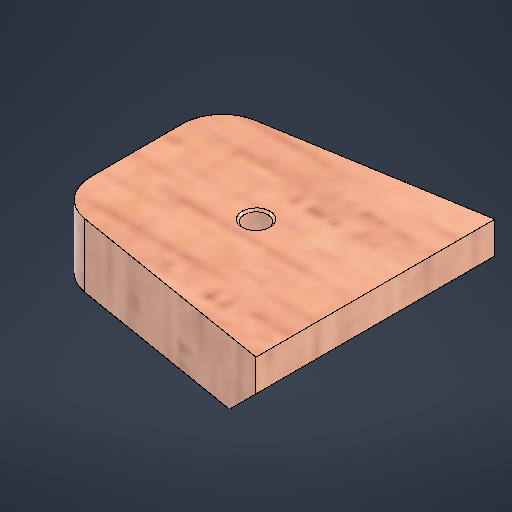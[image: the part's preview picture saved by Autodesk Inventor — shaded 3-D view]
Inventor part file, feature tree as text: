
AUTODESK INVENTOR PART (.ipt)
format: ipt  version: 2025.3 (Build 293356000, 356)  size: 276,480 bytes
history: native  units: mm
features: chamfer x2, sketch x1, extrude x1, hole x1, fillet x1
ambient origin geometry x8: Origin, YZ Plane, XZ Plane, XY Plane, X Axis, Y Axis, Z Axis, Center Point
bodies: Solid1 (feature_tree)
feature tree (6):
  sketch  "Sketch1"  dims[d1=30.0mm d2=30.0mm d3=8.0mm d4=0.0mm d5=3.0mm d6=8.0mm d7=3.5mm d8=6.8mm d9=90.0deg d10=8.0mm d11=20.594885mm d12=0.25mm d13=2.0mm d14=45.0deg d15=5.0mm d19=20.0mm d20=30.0mm d21=4.0mm d22=2.0mm d23=45.0deg]
  extrude  "Extrusion1"  Depth=30.0mm
  hole  "Hole1"  [1 undecoded]
  chamfer  "Chamfer1"  Distance=0.25mm Angle=45.0deg
  fillet  "Fillet1"  Radius=5.0mm
  chamfer  "Chamfer3"  Distance=20.0mm
note: 1 required parameter value undecoded (feature->parameter linkage not recoverable at this tier; creation-order binding heuristic only, values carry confidence <= 0.55)
